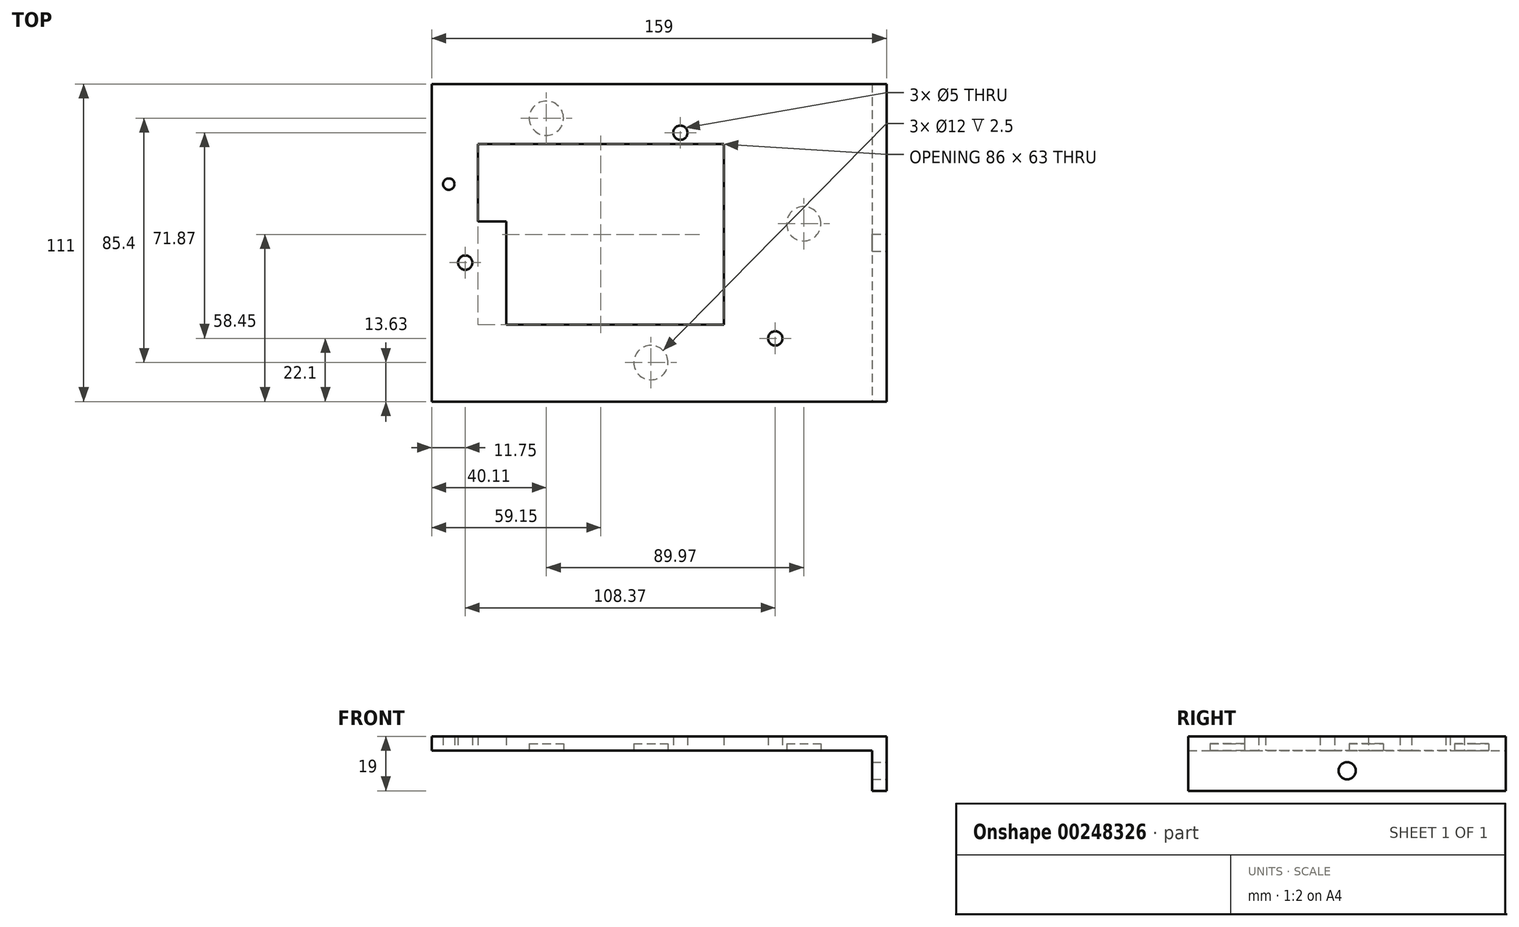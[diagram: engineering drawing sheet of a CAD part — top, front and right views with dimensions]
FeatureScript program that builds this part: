
annotation { "Feature Type Name" : "Feature", "Feature Type Description" : "" }
export const myFeature = defineFeature(function(context is Context, id is Id, definition is map)
    precondition{}
    {
        {
            var Q0;
            Q0=qCreatedBy(makeId("Top.planeOp"),FACE);
            var sketch = newSketch(context, id + "F0", { "sketchPlane" : qUnion([Q0])});
            skLineSegment(sketch, "E0.bottom", {"start": v(0, 0) * mm, "end": v(159, 0) * mm});
            skLineSegment(sketch, "E0.top", {"start": v(0, 111) * mm, "end": v(159, 111) * mm});
            skLineSegment(sketch, "E0.left", {"start": v(0, 0) * mm, "end": v(0, 111) * mm});
            skLineSegment(sketch, "E0.right", {"start": v(159, 0) * mm, "end": v(159, 111) * mm});
            skLineSegment(sketch, "E1", {"start": v(16.15, 89.95) * mm, "end": v(16.15, 62.95) * mm});
            skLineSegment(sketch, "E2", {"start": v(102.15, 89.95) * mm, "end": v(102.15, 26.95) * mm});
            skLineSegment(sketch, "E3", {"start": v(16.15, 89.95) * mm, "end": v(102.15, 89.95) * mm});
            skLineSegment(sketch, "E4", {"start": v(16.15, 62.95) * mm, "end": v(26.15, 62.95) * mm});
            skLineSegment(sketch, "E5", {"start": v(26.15, 62.95) * mm, "end": v(26.15, 26.95) * mm});
            skPoint(sketch, "E6.orphan", {"position": v(16.15, 111) * mm});
            skPoint(sketch, "E7.orphan", {"position": v(102.15, 111) * mm});
            skPoint(sketch, "E8.orphan", {"position": v(102.15, 0) * mm});
            skLineSegment(sketch, "E9.trimOffspring", {"start": v(26.15, 26.95) * mm, "end": v(102.15, 26.95) * mm});
            skPoint(sketch, "E10.start.orphan", {"position": v(0, 26.95) * mm});
            skPoint(sketch, "E11.orphan", {"position": v(16.15, 0) * mm});
            skPoint(sketch, "E12.orphan", {"position": v(0, 89.95) * mm});
            skLineSegment(sketch, "E13", {"start": v(86.95, 119.63) * mm, "end": v(86.95, 91.64) * mm, "construction": true});
            skLineSegment(sketch, "E14", {"start": v(0, 76) * mm, "end": v(25.06, 76) * mm, "construction": true});
            skLineSegment(sketch, "E15", {"start": v(6, 87.5) * mm, "end": v(6, 71.06) * mm, "construction": true});
            skLineSegment(sketch, "E16", {"start": v(0, 48.57) * mm, "end": v(40.1, 48.57) * mm, "construction": true});
            skLineSegment(sketch, "E17", {"start": v(120.12, 36.69) * mm, "end": v(120.12, 7.18) * mm, "construction": true});
            skLineSegment(sketch, "E18", {"start": v(76.7, 93.97) * mm, "end": v(99.03, 93.97) * mm, "construction": true});
            skCircle(sketch, "E19", {"center": v(86.95, 93.97) * mm, "radius": 2.5 * mm});
            skCircle(sketch, "E20", {"center": v(6, 76) * mm, "radius": 2 * mm});
            skLineSegment(sketch, "E21", {"start": v(11.75, 55.2) * mm, "end": v(11.75, 35.72) * mm, "construction": true});
            skCircle(sketch, "E22", {"center": v(11.75, 48.57) * mm, "radius": 2.5 * mm});
            skLineSegment(sketch, "E23", {"start": v(107.63, 22.1) * mm, "end": v(127.42, 22.1) * mm, "construction": true});
            skCircle(sketch, "E24", {"center": v(120.12, 22.1) * mm, "radius": 2.5 * mm});
            skSolve(sketch);
        }
        {
            var Q0;
            Q0=makeQuery(id+"F0.imprint","IMPRINT",FACE,{"disambiguationData":[TD([[makeQuery(id+"F0.imprint","IMPRINT",EDGE,{"derivedFrom":sQuery(id+"F0.wireOp",EDGE,"E0.bottom")}),1.0]])]});
            extrude(context, id + "F1", {"entities" : qUnion([Q0]), "depth" : 5 * mm, "offsetDistance" : 25 * mm});
        }
        {
            var Q0;
            Q0=makeQuery(id+"F1.opExtrude","CAP_FACE",FACE,{"disambiguationData":[OSD([sQuery(id+"F0.wireOp",EDGE,"E0.bottom"),sQuery(id+"F0.wireOp",EDGE,"E0.top"),sQuery(id+"F0.wireOp",EDGE,"E0.left"),sQuery(id+"F0.wireOp",EDGE,"E0.right"),sQuery(id+"F0.wireOp",EDGE,"E1"),sQuery(id+"F0.wireOp",EDGE,"E2"),sQuery(id+"F0.wireOp",EDGE,"E3"),sQuery(id+"F0.wireOp",EDGE,"E4"),sQuery(id+"F0.wireOp",EDGE,"E5"),sQuery(id+"F0.wireOp",EDGE,"E9.trimOffspring"),sQuery(id+"F0.wireOp",EDGE,"E19"),sQuery(id+"F0.wireOp",EDGE,"E20"),sQuery(id+"F0.wireOp",EDGE,"E22"),sQuery(id+"F0.wireOp",EDGE,"E24")])],"isStart":false});
            var sketch = newSketch(context, id + "F2", { "sketchPlane" : qUnion([Q0])});
            skLineSegment(sketch, "E25", {"start": v(154, 111) * mm, "end": v(154, 0) * mm});
            skSolve(sketch);
        }
        {
            var Q0;
            {var subQ0=sQuery(id+"F2.wireOp",EDGE,"E25");Q0=makeQuery(id+"F2.imprint","IMPRINT",FACE,{"disambiguationData":[TD([[makeQuery(id+"F2.imprint","IMPRINT",EDGE,{"derivedFrom":subQ0}),1.0]])]});}
            extrude(context, id + "F3", {"entities" : qUnion([Q0]), "operationType" : NewBodyOperationType.ADD, "oppositeDirection" : true, "depth" : 19 * mm, "offsetDistance" : 25 * mm});
        }
        {
            var Q0;
            {var subQ0=sQuery(id+"F0.wireOp",EDGE,"E0.right");Q0=makeQuery(id+"F3.boolean.opBoolean","MERGE",FACE,{"derivedFrom":[makeQuery(id+"F1.opExtrude","SWEPT_FACE",FACE,{"disambiguationData":[OSD([subQ0])]}),makeQuery(id+"F3.opExtrude","SWEPT_FACE",FACE,{"disambiguationData":[OSD([subQ0])]})]});}
            var sketch = newSketch(context, id + "F4", { "sketchPlane" : qUnion([Q0])});
            skLineSegment(sketch, "E26", {"start": v(55.5, -14) * mm, "end": v(55.5, 5) * mm, "construction": true});
            skLineSegment(sketch, "E27", {"start": v(41, -7) * mm, "end": v(69.65, -7) * mm, "construction": true});
            skCircle(sketch, "E28", {"center": v(55.5, -7) * mm, "radius": 3 * mm});
            skSolve(sketch);
        }
        {
            var Q0;
            Q0=makeQuery(id+"F4.imprint","IMPRINT",FACE,{"disambiguationData":[TD([[makeQuery(id+"F4.imprint","IMPRINT",EDGE,{"derivedFrom":sQuery(id+"F4.wireOp",EDGE,"E28")}),1.0]])]});
            extrude(context, id + "F5", {"entities" : qUnion([Q0]), "operationType" : NewBodyOperationType.REMOVE, "oppositeDirection" : true, "depth" : 5 * mm, "offsetDistance" : 25 * mm});
        }
        {
            var Q0;
            Q0=makeQuery(id+"F1.opExtrude","CAP_FACE",FACE,{"disambiguationData":[OSD([sQuery(id+"F0.wireOp",EDGE,"E0.bottom"),sQuery(id+"F0.wireOp",EDGE,"E0.top"),sQuery(id+"F0.wireOp",EDGE,"E0.left"),sQuery(id+"F0.wireOp",EDGE,"E0.right"),sQuery(id+"F0.wireOp",EDGE,"E1"),sQuery(id+"F0.wireOp",EDGE,"E2"),sQuery(id+"F0.wireOp",EDGE,"E3"),sQuery(id+"F0.wireOp",EDGE,"E4"),sQuery(id+"F0.wireOp",EDGE,"E5"),sQuery(id+"F0.wireOp",EDGE,"E9.trimOffspring"),sQuery(id+"F0.wireOp",EDGE,"E19"),sQuery(id+"F0.wireOp",EDGE,"E20"),sQuery(id+"F0.wireOp",EDGE,"E22"),sQuery(id+"F0.wireOp",EDGE,"E24")])],"isStart":true});
            var sketch = newSketch(context, id + "F6", { "sketchPlane" : qUnion([Q0])});
            skLineSegment(sketch, "E29", {"start": v(117.92, -62.15) * mm, "end": v(154, -62.15) * mm, "construction": true});
            skLineSegment(sketch, "E30", {"start": v(130.08, -44.44) * mm, "end": v(130.08, -83.56) * mm, "construction": true});
            skCircle(sketch, "E31", {"center": v(130.08, -62.15) * mm, "radius": 6 * mm});
            skLineSegment(sketch, "E32", {"start": v(57.56, -13.63) * mm, "end": v(96.13, -13.63) * mm, "construction": true});
            skLineSegment(sketch, "E33", {"start": v(76.65, 0) * mm, "end": v(76.65, -24.34) * mm, "construction": true});
            skCircle(sketch, "E34", {"center": v(76.65, -13.63) * mm, "radius": 6 * mm});
            skLineSegment(sketch, "E35", {"start": v(40.1, -93.48) * mm, "end": v(40.1, -111) * mm, "construction": true});
            skLineSegment(sketch, "E36", {"start": v(22.03, -99.03) * mm, "end": v(56.46, -99.03) * mm, "construction": true});
            skCircle(sketch, "E37", {"center": v(40.1, -99.03) * mm, "radius": 6 * mm});
            skSolve(sketch);
        }
        {
            var Q0;
            Q0=makeQuery(id+"F6.imprint","IMPRINT",FACE,{"disambiguationData":[TD([[makeQuery(id+"F6.imprint","IMPRINT",EDGE,{"derivedFrom":sQuery(id+"F6.wireOp",EDGE,"E34")}),1.0]])]});
            var Q1;
            Q1=makeQuery(id+"F6.imprint","IMPRINT",FACE,{"disambiguationData":[TD([[makeQuery(id+"F6.imprint","IMPRINT",EDGE,{"derivedFrom":sQuery(id+"F6.wireOp",EDGE,"E31")}),1.0]])]});
            var Q2;
            Q2=makeQuery(id+"F6.imprint","IMPRINT",FACE,{"disambiguationData":[TD([[makeQuery(id+"F6.imprint","IMPRINT",EDGE,{"derivedFrom":sQuery(id+"F6.wireOp",EDGE,"E37")}),1.0]])]});
            extrude(context, id + "F7", {"entities" : qUnion([Q0, Q1, Q2]), "operationType" : NewBodyOperationType.REMOVE, "oppositeDirection" : true, "depth" : 2.5 * mm, "offsetDistance" : 25 * mm});
        }
    });
